# Revit family: Serene_T&T_Window_C_Standard
name_source: partatom
category: Windows
revit_build: Autodesk Revit 2014 (Build: 20130308_1515(x64)
units: mm (PartAtom-declared; Revit-internal decimal feet)

## types (12) — shared parameters
Centered In Wall = Yes
Custom Sash Width = 522 mm  [stored 1.7126 ft]
DG Gasket Finish = Double Glazing Gasket Material
DG Gasket Tickness = 12 mm  [stored 0.0393701 ft]
DG Thickness Calc = 4 mm  [stored 0.0131234 ft]
Default Sill Height = 800 mm  [stored 2.62467 ft]
Description = Tilt and turn window, Type C
Frame Thickness = 52 mm
Frame Width = 62 mm  [stored 0.203412 ft]
Limit Fixed Pane Height Min = 200 mm  [stored 0.656168 ft]
Limit Fixed Panel Width Max = 1800 mm  [stored 5.90551 ft]
Limit Fixed Panel Width Min = 200 mm  [stored 0.656168 ft]
Limit Sash Height Max = 1500 mm  [stored 4.92126 ft]
Limit Sash Height Min = 300 mm  [stored 0.984252 ft]
Limit Sash Width Max = 700 mm  [stored 2.29659 ft]
Limit Sash Width Min = 300 mm  [stored 0.984252 ft]
Limit Window Height Max = 1568 mm  [stored 5.14436 ft]
Limit Window Height Min = 368 mm  [stored 1.20735 ft]
Limit Window Width Max = 2979 mm
Limit Window Width Min = 1379 mm
Manufacturer = Crealco
Max System DG One Piece Thickness = 4 mm  [stored 0.0131234 ft]
Max System DG Unit Thickness = 20 mm  [stored 0.0656168 ft]
Model = Serene
Mullion Side Spacing = 528 mm  [stored 1.73228 ft]
Sash Edge Gap = 34 mm
Sash Frame Gasket = 3 mm  [stored 0.00984252 ft]
Sash Overlap = 28 mm  [stored 0.0918635 ft]
Sash Width = 522 mm  [stored 1.7126 ft]
URL = http://www.crealco.co.za
Wall Closure = By host
zero-valued in all types: Custom Window Exterior Offset

## per-type parameters (varying)
- 52TT-1809SS-1000Pa: Area Glazing Fixed Panel=0.48 m²; Area Glazing Sash=0.3 m²; Clearvue Insulated LowE SHGC Value=0.424; Clearvue Insulated LowE U Value=3.99; Clearvue Insulated SHGC Value=0.464; Clearvue Insulated U Value=4.43; Clearvue SHGC Value=0.525; Clearvue U Value=6.34; Custom Windload=1000 mm  [stored 3.28084 ft]; Custom Window Height=890 mm  [stored 2.91995 ft]; Custom Window Width=1790 mm  [stored 5.8727 ft]; Energy Advantage SHGC Value=0.471; Energy Advantage U Value=5.45; Fixed Panel Height=810 mm; Fixed Panel Width=611 mm; Height=890 mm  [stored 2.91995 ft]; Intruderprufe LowE SHGC Value=0.431; Intruderprufe LowE U Value=4.63; Intruderprufe SHGC Value=0.486; Intruderprufe U Value=6.23; Length Mullion=810 mm; Max Pane Area=0.48 m²; Sash Height=822 mm  [stored 2.69685 ft]; Width=1790 mm  [stored 5.8727 ft]; Windload Design=1000 mm  [stored 3.28084 ft]
- 52TT-1809SS-1500Pa: Area Glazing Fixed Panel=0.48 m²; Area Glazing Sash=0.3 m²; Clearvue Insulated LowE SHGC Value=0.424; Clearvue Insulated LowE U Value=3.99; Clearvue Insulated SHGC Value=0.464; Clearvue Insulated U Value=4.43; Clearvue SHGC Value=0.525; Clearvue U Value=6.34; Custom Windload=1500 mm  [stored 4.92126 ft]; Custom Window Height=890 mm  [stored 2.91995 ft]; Custom Window Width=1790 mm  [stored 5.8727 ft]; Energy Advantage SHGC Value=0.471; Energy Advantage U Value=5.45; Fixed Panel Height=810 mm; Fixed Panel Width=611 mm; Height=890 mm  [stored 2.91995 ft]; Intruderprufe LowE SHGC Value=0.431; Intruderprufe LowE U Value=4.63; Intruderprufe SHGC Value=0.486; Intruderprufe U Value=6.23; Length Mullion=810 mm; Max Pane Area=0.48 m²; Sash Height=822 mm  [stored 2.69685 ft]; Width=1790 mm  [stored 5.8727 ft]; Windload Design=1500 mm  [stored 4.92126 ft]
- 52TT-1809SS-2000Pa: Area Glazing Fixed Panel=0.48 m²; Area Glazing Sash=0.3 m²; Clearvue Insulated LowE SHGC Value=0.424; Clearvue Insulated LowE U Value=3.99; Clearvue Insulated SHGC Value=0.464; Clearvue Insulated U Value=4.43; Clearvue SHGC Value=0.525; Clearvue U Value=6.34; Custom Windload=2000 mm  [stored 6.56168 ft]; Custom Window Height=890 mm  [stored 2.91995 ft]; Custom Window Width=1790 mm  [stored 5.8727 ft]; Energy Advantage SHGC Value=0.471; Energy Advantage U Value=5.45; Fixed Panel Height=810 mm; Fixed Panel Width=611 mm; Height=890 mm  [stored 2.91995 ft]; Intruderprufe LowE SHGC Value=0.431; Intruderprufe LowE U Value=4.63; Intruderprufe SHGC Value=0.486; Intruderprufe U Value=6.23; Length Mullion=810 mm; Max Pane Area=0.48 m²; Sash Height=822 mm  [stored 2.69685 ft]; Width=1790 mm  [stored 5.8727 ft]; Windload Design=2000 mm  [stored 6.56168 ft]
- 52TT-2409SS-1000Pa: Area Glazing Fixed Panel=0.96 m²; Area Glazing Sash=0.3 m²; Clearvue Insulated LowE SHGC Value=0.464; Clearvue Insulated LowE U Value=3.65; Clearvue Insulated SHGC Value=0.509; Clearvue Insulated U Value=4.15; Clearvue SHGC Value=0.576; Clearvue U Value=6.24; Custom Windload=1000 mm  [stored 3.28084 ft]; Custom Window Height=890 mm  [stored 2.91995 ft]; Custom Window Width=2390 mm  [stored 7.84121 ft]; Energy Advantage SHGC Value=0.517; Energy Advantage U Value=5.2; Fixed Panel Height=810 mm; Fixed Panel Width=1211 mm; Height=890 mm  [stored 2.91995 ft]; Intruderprufe LowE SHGC Value=0.473; Intruderprufe LowE U Value=4.55; Intruderprufe SHGC Value=0.534; Intruderprufe U Value=6.12; Length Mullion=810 mm; Max Pane Area=0.96 m²; Sash Height=822 mm  [stored 2.69685 ft]; Width=2390 mm  [stored 7.84121 ft]; Windload Design=1000 mm  [stored 3.28084 ft]
- 52TT-2409SS-1500Pa: Area Glazing Fixed Panel=0.96 m²; Area Glazing Sash=0.3 m²; Clearvue Insulated LowE SHGC Value=0.464; Clearvue Insulated LowE U Value=3.65; Clearvue Insulated SHGC Value=0.509; Clearvue Insulated U Value=4.15; Clearvue SHGC Value=0.576; Clearvue U Value=6.24; Custom Windload=1500 mm  [stored 4.92126 ft]; Custom Window Height=890 mm  [stored 2.91995 ft]; Custom Window Width=2390 mm  [stored 7.84121 ft]; Energy Advantage SHGC Value=0.517; Energy Advantage U Value=5.2; Fixed Panel Height=810 mm; Fixed Panel Width=1211 mm; Height=890 mm  [stored 2.91995 ft]; Intruderprufe LowE SHGC Value=0.473; Intruderprufe LowE U Value=4.55; Intruderprufe SHGC Value=0.534; Intruderprufe U Value=6.12; Length Mullion=810 mm; Max Pane Area=0.96 m²; Sash Height=822 mm  [stored 2.69685 ft]; Width=2390 mm  [stored 7.84121 ft]; Windload Design=1500 mm  [stored 4.92126 ft]
- 52TT-2409SS-2000Pa: Area Glazing Fixed Panel=0.96 m²; Area Glazing Sash=0.3 m²; Clearvue Insulated LowE SHGC Value=0.464; Clearvue Insulated LowE U Value=3.65; Clearvue Insulated SHGC Value=0.509; Clearvue Insulated U Value=4.15; Clearvue SHGC Value=0.576; Clearvue U Value=6.24; Custom Windload=2000 mm  [stored 6.56168 ft]; Custom Window Height=890 mm  [stored 2.91995 ft]; Custom Window Width=2390 mm  [stored 7.84121 ft]; Energy Advantage SHGC Value=0.517; Energy Advantage U Value=5.2; Fixed Panel Height=810 mm; Fixed Panel Width=1211 mm; Height=890 mm  [stored 2.91995 ft]; Intruderprufe LowE SHGC Value=0.473; Intruderprufe LowE U Value=4.55; Intruderprufe SHGC Value=0.534; Intruderprufe U Value=6.12; Length Mullion=810 mm; Max Pane Area=0.96 m²; Sash Height=822 mm  [stored 2.69685 ft]; Width=2390 mm  [stored 7.84121 ft]; Windload Design=2000 mm  [stored 6.56168 ft]
- 52TT-1812SS-1000Pa: Area Glazing Fixed Panel=0.66 m²; Area Glazing Sash=0.43 m²; Clearvue Insulated LowE SHGC Value=0.446; Clearvue Insulated LowE U Value=3.81; Clearvue Insulated SHGC Value=0.4889; Clearvue Insulated U Value=4.27; Clearvue SHGC Value=0.553; Clearvue U Value=6.28; Custom Windload=1000 mm  [stored 3.28084 ft]; Custom Window Height=1190 mm  [stored 3.9042 ft]; Custom Window Width=1790 mm  [stored 5.8727 ft]; Energy Advantage SHGC Value=0.497; Energy Advantage U Value=5.31; Fixed Panel Height=1110 mm  [stored 3.64173 ft]; Fixed Panel Width=611 mm; Height=1190 mm  [stored 3.9042 ft]; Intruderprufe LowE SHGC Value=0.455; Intruderprufe LowE U Value=4.58; Intruderprufe SHGC Value=0.513; Intruderprufe U Value=6.16; Length Mullion=1110 mm  [stored 3.64173 ft]; Max Pane Area=0.66 m²; Sash Height=1122 mm  [stored 3.6811 ft]; Width=1790 mm  [stored 5.8727 ft]; Windload Design=1000 mm  [stored 3.28084 ft]
- 52TT-1812SS-1500Pa: Area Glazing Fixed Panel=0.66 m²; Area Glazing Sash=0.43 m²; Clearvue Insulated LowE SHGC Value=0.446; Clearvue Insulated LowE U Value=3.81; Clearvue Insulated SHGC Value=0.4889; Clearvue Insulated U Value=4.27; Clearvue SHGC Value=0.553; Clearvue U Value=6.28; Custom Windload=1500 mm  [stored 4.92126 ft]; Custom Window Height=1190 mm  [stored 3.9042 ft]; Custom Window Width=1790 mm  [stored 5.8727 ft]; Energy Advantage SHGC Value=0.497; Energy Advantage U Value=5.31; Fixed Panel Height=1110 mm  [stored 3.64173 ft]; Fixed Panel Width=611 mm; Height=1190 mm  [stored 3.9042 ft]; Intruderprufe LowE SHGC Value=0.455; Intruderprufe LowE U Value=4.58; Intruderprufe SHGC Value=0.513; Intruderprufe U Value=6.16; Length Mullion=1110 mm  [stored 3.64173 ft]; Max Pane Area=0.66 m²; Sash Height=1122 mm  [stored 3.6811 ft]; Width=1790 mm  [stored 5.8727 ft]; Windload Design=1500 mm  [stored 4.92126 ft]
- 52TT-1812SS-2000Pa: Area Glazing Fixed Panel=0.66 m²; Area Glazing Sash=0.43 m²; Clearvue Insulated LowE SHGC Value=0.446; Clearvue Insulated LowE U Value=3.81; Clearvue Insulated SHGC Value=0.4889; Clearvue Insulated U Value=4.27; Clearvue SHGC Value=0.553; Clearvue U Value=6.28; Custom Windload=2000 mm  [stored 6.56168 ft]; Custom Window Height=1190 mm  [stored 3.9042 ft]; Custom Window Width=1790 mm  [stored 5.8727 ft]; Energy Advantage SHGC Value=0.497; Energy Advantage U Value=5.31; Fixed Panel Height=1110 mm  [stored 3.64173 ft]; Fixed Panel Width=611 mm; Height=1190 mm  [stored 3.9042 ft]; Intruderprufe LowE SHGC Value=0.455; Intruderprufe LowE U Value=4.58; Intruderprufe SHGC Value=0.513; Intruderprufe U Value=6.16; Length Mullion=1110 mm  [stored 3.64173 ft]; Max Pane Area=0.66 m²; Sash Height=1122 mm  [stored 3.6811 ft]; Width=1790 mm  [stored 5.8727 ft]; Windload Design=2000 mm  [stored 6.56168 ft]
- 52TT-2412SS-1000Pa: Area Glazing Fixed Panel=1.32 m²; Area Glazing Sash=0.43 m²; Clearvue Insulated LowE SHGC Value=0.446; Clearvue Insulated LowE U Value=3.81; Clearvue Insulated SHGC Value=0.4889; Clearvue Insulated U Value=4.27; Clearvue SHGC Value=0.553; Clearvue U Value=6.28; Custom Windload=1000 mm  [stored 3.28084 ft]; Custom Window Height=1190 mm  [stored 3.9042 ft]; Custom Window Width=2390 mm  [stored 7.84121 ft]; Energy Advantage SHGC Value=0.497; Energy Advantage U Value=5.31; Fixed Panel Height=1110 mm  [stored 3.64173 ft]; Fixed Panel Width=1211 mm; Height=1190 mm  [stored 3.9042 ft]; Intruderprufe LowE SHGC Value=0.455; Intruderprufe LowE U Value=4.58; Intruderprufe SHGC Value=0.513; Intruderprufe U Value=6.16; Length Mullion=1110 mm  [stored 3.64173 ft]; Max Pane Area=1.32 m²; Sash Height=1122 mm  [stored 3.6811 ft]; Width=2390 mm  [stored 7.84121 ft]; Windload Design=1000 mm  [stored 3.28084 ft]
- 52TT-2412SS-1500Pa: Area Glazing Fixed Panel=1.32 m²; Area Glazing Sash=0.43 m²; Clearvue Insulated LowE SHGC Value=0.446; Clearvue Insulated LowE U Value=3.81; Clearvue Insulated SHGC Value=0.4889; Clearvue Insulated U Value=4.27; Clearvue SHGC Value=0.553; Clearvue U Value=6.28; Custom Windload=1500 mm  [stored 4.92126 ft]; Custom Window Height=1190 mm  [stored 3.9042 ft]; Custom Window Width=2390 mm  [stored 7.84121 ft]; Energy Advantage SHGC Value=0.497; Energy Advantage U Value=5.31; Fixed Panel Height=1110 mm  [stored 3.64173 ft]; Fixed Panel Width=1211 mm; Height=1190 mm  [stored 3.9042 ft]; Intruderprufe LowE SHGC Value=0.455; Intruderprufe LowE U Value=4.58; Intruderprufe SHGC Value=0.513; Intruderprufe U Value=6.16; Length Mullion=1110 mm  [stored 3.64173 ft]; Max Pane Area=1.32 m²; Sash Height=1122 mm  [stored 3.6811 ft]; Width=2390 mm  [stored 7.84121 ft]; Windload Design=1500 mm  [stored 4.92126 ft]
- 52TT-2412SS-2000Pa: Area Glazing Fixed Panel=1.32 m²; Area Glazing Sash=0.43 m²; Clearvue Insulated LowE SHGC Value=0.446; Clearvue Insulated LowE U Value=3.81; Clearvue Insulated SHGC Value=0.4889; Clearvue Insulated U Value=4.27; Clearvue SHGC Value=0.553; Clearvue U Value=6.28; Custom Windload=2000 mm  [stored 6.56168 ft]; Custom Window Height=1190 mm  [stored 3.9042 ft]; Custom Window Width=2390 mm  [stored 7.84121 ft]; Energy Advantage SHGC Value=0.497; Energy Advantage U Value=5.31; Fixed Panel Height=1110 mm  [stored 3.64173 ft]; Fixed Panel Width=1211 mm; Height=1190 mm  [stored 3.9042 ft]; Intruderprufe LowE SHGC Value=0.455; Intruderprufe LowE U Value=4.58; Intruderprufe SHGC Value=0.513; Intruderprufe U Value=6.16; Length Mullion=1110 mm  [stored 3.64173 ft]; Max Pane Area=1.32 m²; Sash Height=1122 mm  [stored 3.6811 ft]; Width=2390 mm  [stored 7.84121 ft]; Windload Design=2000 mm  [stored 6.56168 ft]

note: [stored X ft] marks values corroborated as IEEE doubles in the binary element streams (Revit-internal decimal feet)

## geometry (parser evidence)
native form markers: Sweep x30
no freeform markers — native parametric forms only
